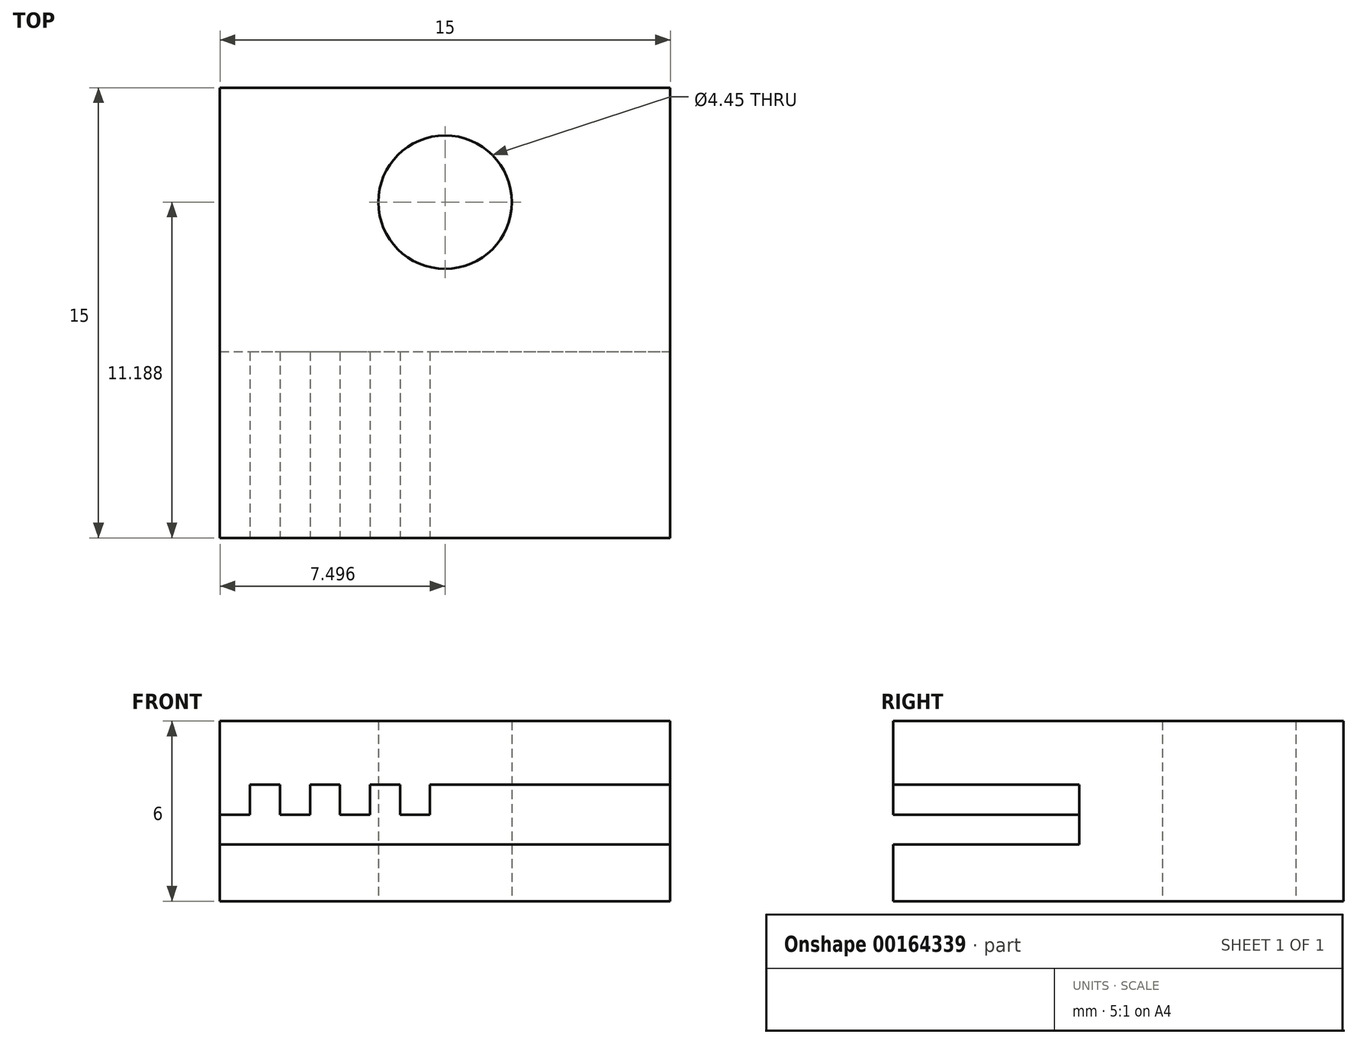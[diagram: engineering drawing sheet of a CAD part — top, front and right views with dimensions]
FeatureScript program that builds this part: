
annotation { "Feature Type Name" : "Feature", "Feature Type Description" : "" }
export const myFeature = defineFeature(function(context is Context, id is Id, definition is map)
    precondition{}
    {
        {
            var Q0;
            Q0=qCreatedBy(makeId("Top.planeOp"),FACE);
            var sketch = newSketch(context, id + "F0", { "sketchPlane" : qUnion([Q0])});
            skLineSegment(sketch, "E0.bottom", {"start": v(6.14, 10.11) * mm, "end": v(21.14, 10.11) * mm});
            skLineSegment(sketch, "E0.top", {"start": v(6.14, -4.89) * mm, "end": v(21.14, -4.89) * mm});
            skLineSegment(sketch, "E0.left", {"start": v(6.14, 10.11) * mm, "end": v(6.14, -4.89) * mm});
            skLineSegment(sketch, "E0.right", {"start": v(21.14, 10.11) * mm, "end": v(21.14, -4.89) * mm});
            skSolve(sketch);
        }
        {
            var Q0;
            Q0=qSketchRegion(id+"F0",true);
            extrude(context, id + "F1", {"entities" : qUnion([Q0]), "depth" : 6 * mm});
        }
        {
            var Q0;
            Q0=makeQuery(id+"F1.opExtrude","SWEPT_FACE",FACE,{"disambiguationData":[OSD([sQuery(id+"F0.wireOp",EDGE,"E0.top")])]});
            var sketch = newSketch(context, id + "F2", { "sketchPlane" : qUnion([Q0])});
            skLineSegment(sketch, "E1", {"start": v(6.14, 1.88) * mm, "end": v(21.14, 1.88) * mm});
            skLineSegment(sketch, "E2", {"start": v(6.14, 2.88) * mm, "end": v(7.14, 2.88) * mm});
            skLineSegment(sketch, "E3", {"start": v(7.14, 2.88) * mm, "end": v(7.14, 3.88) * mm});
            skLineSegment(sketch, "E4", {"start": v(7.14, 3.88) * mm, "end": v(8.14, 3.88) * mm});
            skLineSegment(sketch, "E5", {"start": v(8.14, 3.88) * mm, "end": v(8.14, 2.88) * mm});
            skLineSegment(sketch, "E6.1.0.0", {"start": v(10.14, 3.88) * mm, "end": v(10.14, 2.88) * mm});
            skLineSegment(sketch, "E6.1.0.1", {"start": v(9.14, 3.88) * mm, "end": v(10.14, 3.88) * mm});
            skLineSegment(sketch, "E6.1.0.2", {"start": v(9.14, 2.88) * mm, "end": v(9.14, 3.88) * mm});
            skLineSegment(sketch, "E6.1.0.3", {"start": v(8.14, 2.88) * mm, "end": v(9.14, 2.88) * mm});
            skLineSegment(sketch, "E6.2.0.0", {"start": v(12.14, 3.88) * mm, "end": v(12.14, 2.88) * mm});
            skLineSegment(sketch, "E6.2.0.1", {"start": v(11.14, 3.88) * mm, "end": v(12.14, 3.88) * mm});
            skLineSegment(sketch, "E6.2.0.2", {"start": v(11.14, 2.88) * mm, "end": v(11.14, 3.88) * mm});
            skLineSegment(sketch, "E6.2.0.3", {"start": v(10.14, 2.88) * mm, "end": v(11.14, 2.88) * mm});
            skLineSegment(sketch, "E6.3.0.1", {"start": v(13.14, 3.88) * mm, "end": v(14.14, 3.88) * mm});
            skLineSegment(sketch, "E6.3.0.2", {"start": v(13.14, 2.88) * mm, "end": v(13.14, 3.88) * mm});
            skLineSegment(sketch, "E6.3.0.3", {"start": v(12.14, 2.88) * mm, "end": v(13.14, 2.88) * mm});
            skLineSegment(sketch, "E6.direction1", {"start": v(6.14, 2.88) * mm, "end": v(8.14, 2.88) * mm, "construction": true});
            skLineSegment(sketch, "E7", {"start": v(14.14, 3.88) * mm, "end": v(21.14, 3.88) * mm});
            skSolve(sketch);
        }
        {
            var Q0;
            {var subQ1=sQuery(id+"F2.wireOp",EDGE,"E1");Q0=makeQuery(id+"F2.imprint","IMPRINT",FACE,{"disambiguationData":[TD([[makeQuery(id+"F2.imprint","IMPRINT",EDGE,{"derivedFrom":subQ1}),1.0]])]});}
            extrude(context, id + "F3", {"entities" : qUnion([Q0]), "operationType" : NewBodyOperationType.REMOVE, "oppositeDirection" : true, "depth" : 6.2 * mm});
        }
        {
            var Q0;
            Q0=makeQuery(id+"F1.opExtrude","CAP_FACE",FACE,{"disambiguationData":[OSD([sQuery(id+"F0.wireOp",EDGE,"E0.bottom"),sQuery(id+"F0.wireOp",EDGE,"E0.top"),sQuery(id+"F0.wireOp",EDGE,"E0.left"),sQuery(id+"F0.wireOp",EDGE,"E0.right")])],"isStart":true});
            var sketch = newSketch(context, id + "F4", { "sketchPlane" : qUnion([Q0])});
            skCircle(sketch, "E8", {"center": v(13.64, -6.3) * mm, "radius": 2.22 * mm});
            skPoint(sketch, "E8.centerSnap0", {"position": v(13.64, -10.11) * mm});
            skSolve(sketch);
        }
        {
            var Q0;
            Q0 = qSketchRegion(id + "F4", true);
            extrude(context, id + "F5", {"entities" : qUnion([Q0]), "operationType" : NewBodyOperationType.REMOVE, "oppositeDirection" : true, "depth" : 25 * mm});
        }
    });
